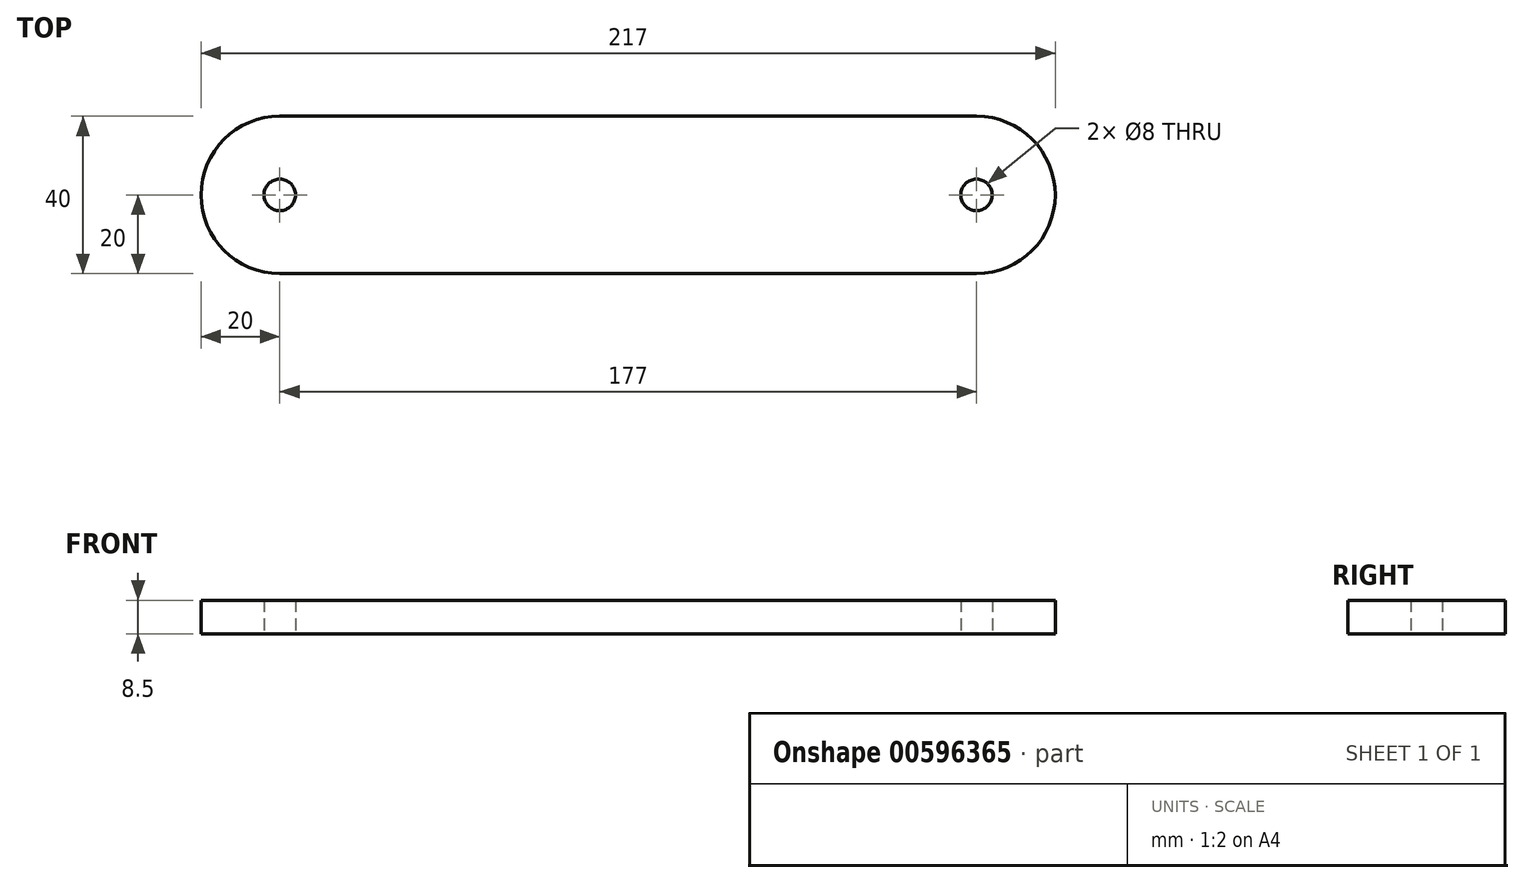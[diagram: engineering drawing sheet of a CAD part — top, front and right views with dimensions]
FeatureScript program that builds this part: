
annotation { "Feature Type Name" : "Feature", "Feature Type Description" : "" }
export const myFeature = defineFeature(function(context is Context, id is Id, definition is map)
    precondition{}
    {
        {
            var Q0;
            Q0=qCreatedBy(makeId("Top.planeOp"),FACE);
            var sketch = newSketch(context, id + "F0", { "sketchPlane" : qUnion([Q0])});
            skLineSegment(sketch, "E0.bottom", {"start": v(88.5, -20) * mm, "end": v(-88.5, -20) * mm});
            skLineSegment(sketch, "E0.top", {"start": v(88.5, 20) * mm, "end": v(-88.5, 20) * mm});
            skPoint(sketch, "E0.middle", {"position": v(0, 0) * mm});
            skCircle(sketch, "E1", {"center": v(-88.5, 0) * mm, "radius": 4 * mm});
            skCircle(sketch, "E2", {"center": v(88.5, 0) * mm, "radius": 4 * mm});
            skArc(sketch, "E3", {"start": v(-88.5, 20) * mm, "mid": v(-108.5, 0) * mm, "end": v(-88.5, -20) * mm});
            skArc(sketch, "E4", {"start": v(88.5, -20) * mm, "mid": v(108.5, 0) * mm, "end": v(88.5, 20) * mm});
            skLineSegment(sketch, "E5", {"start": v(-88.5, -43.17) * mm, "end": v(-88.5, 42.46) * mm, "construction": true});
            skLineSegment(sketch, "E6", {"start": v(88.5, 43.55) * mm, "end": v(88.5, -50.82) * mm, "construction": true});
            skSolve(sketch);
        }
        {
            var Q0;
            Q0 = qSketchRegion(id + "F0", true);
            extrude(context, id + "F1", {"entities" : qUnion([Q0]), "endBound" : BoundingType.SYMMETRIC, "depth" : 8.5 * mm, "offsetDistance" : 25 * mm});
        }
    });
